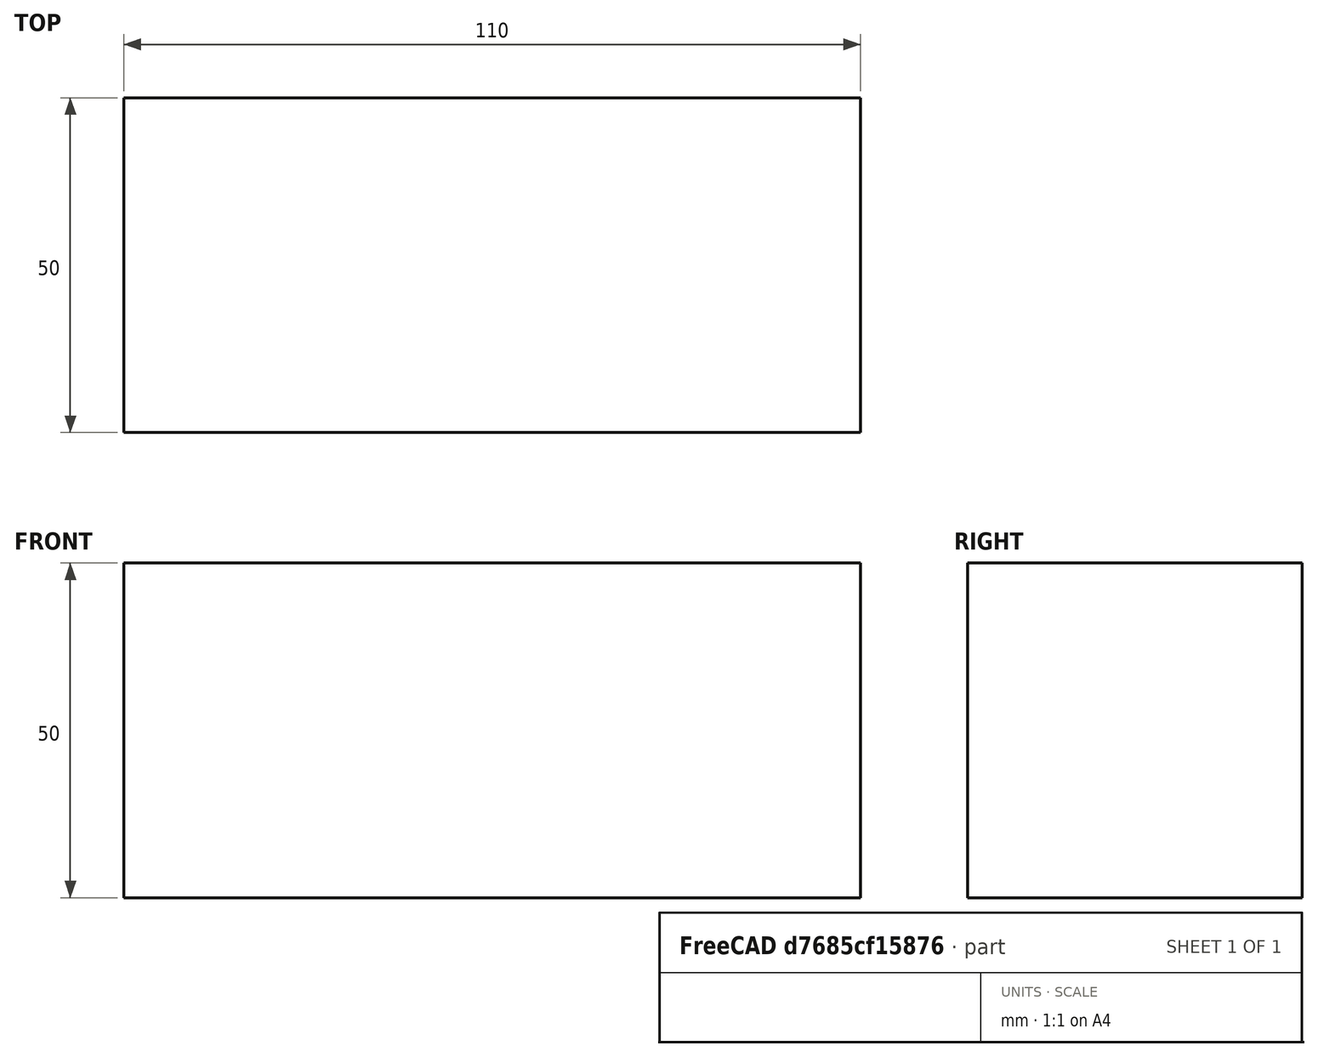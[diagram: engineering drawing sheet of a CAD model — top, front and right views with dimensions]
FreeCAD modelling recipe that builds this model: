
FCSTD DOCUMENT  (FreeCAD 0.15R4671 (Git))
Label: Flat Bar 110x50 EN10058 S235JR
License: All rights reserved
LicenseURL: http://en.wikipedia.org/wiki/All_rights_reserved
objects: Sketcher::SketchObject×1, Part::Extrusion×1
note: 2 computed .brp shape members not serialized (recipe doc carries the construction recipe); baked Part::Feature solids carry a one-line shape summary decoded from their .brp

FEATURE [Sketcher::SketchObject] Sketch
  sketch-geometry (4):
    g0: LineSegment StartX=-55 StartY=-25 StartZ=0 EndX=55 EndY=-25 EndZ=0
    g1: LineSegment StartX=55 StartY=-25 StartZ=0 EndX=55 EndY=25 EndZ=0
    g2: LineSegment StartX=55 StartY=25 StartZ=0 EndX=-55 EndY=25 EndZ=0
    g3: LineSegment StartX=-55 StartY=25 StartZ=0 EndX=-55 EndY=-25 EndZ=0
  constraints (12):
    c: Coincident(g0,g1)
    c: Coincident(g1,g2)
    c: Coincident(g2,g3)
    c: Coincident(g3,g0)
    c: Horizontal(g0)
    c: Horizontal(g2)
    c: Vertical(g1)
    c: Vertical(g3)
    c: Symmetric(g1,g2,g-2)
    c: Symmetric(g0,g1,g-1)
    c: DistanceY(g1) = 50
    c: DistanceX(g0) = 110
FEATURE [Part::Extrusion] Extrude  label="Flat Bar 110x50 EN10058 S235JR"
  Base = -> Sketch
  Dir = (0,0,50)
  Solid = true
